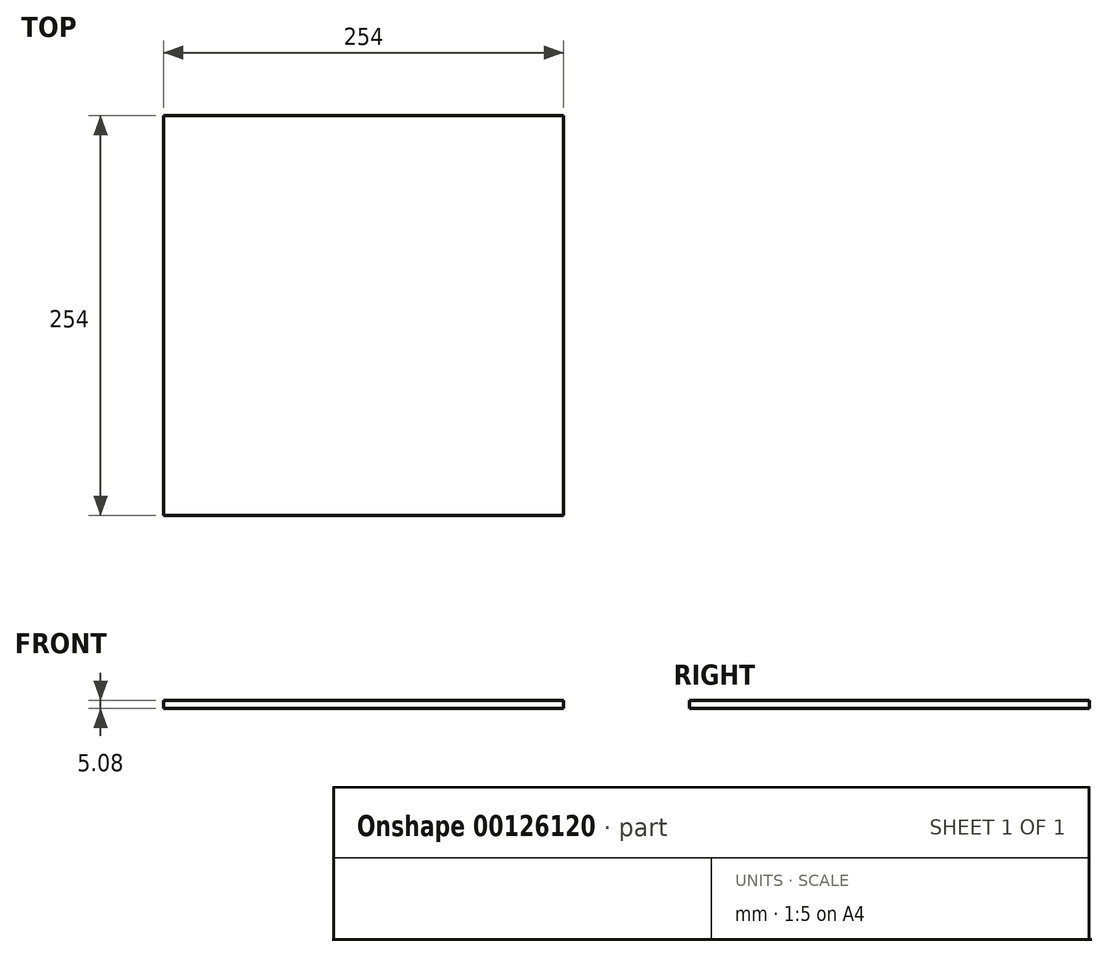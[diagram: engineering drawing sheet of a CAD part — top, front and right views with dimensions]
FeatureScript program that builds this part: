
annotation { "Feature Type Name" : "Feature", "Feature Type Description" : "" }
export const myFeature = defineFeature(function(context is Context, id is Id, definition is map)
    precondition{}
    {
        {
            var Q0;
            Q0=qCreatedBy(makeId("Top.planeOp"),FACE);
            var sketch = newSketch(context, id + "F0", { "sketchPlane" : qUnion([Q0])});
            skLineSegment(sketch, "E0.bottom", {"start": v(-87.53, -64.38) * mm, "end": v(166.47, -64.38) * mm});
            skLineSegment(sketch, "E0.top", {"start": v(-87.53, 189.62) * mm, "end": v(166.47, 189.62) * mm});
            skLineSegment(sketch, "E0.left", {"start": v(-87.53, -64.38) * mm, "end": v(-87.53, 189.62) * mm});
            skLineSegment(sketch, "E0.right", {"start": v(166.47, -64.38) * mm, "end": v(166.47, 189.62) * mm});
            skSolve(sketch);
        }
        {
            var Q0;
            Q0 = qSketchRegion(id + "F0", true);
            extrude(context, id + "F1", {"entities" : qUnion([Q0]), "depth" : 5.08 * mm});
        }
    });
